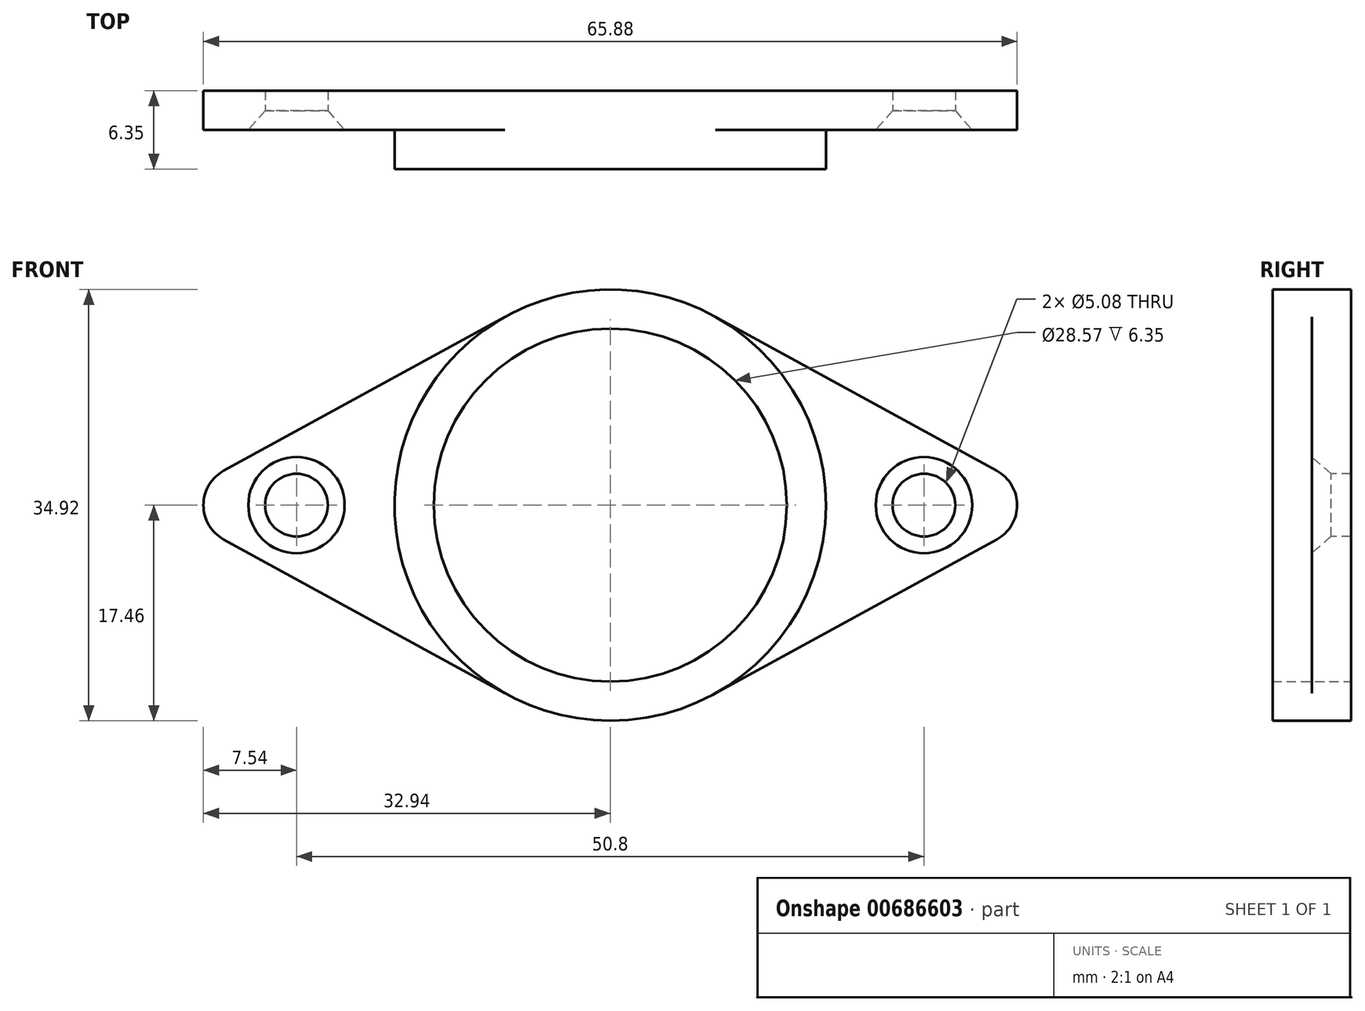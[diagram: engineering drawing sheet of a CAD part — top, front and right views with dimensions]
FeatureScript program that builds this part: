
annotation { "Feature Type Name" : "Feature", "Feature Type Description" : "" }
export const myFeature = defineFeature(function(context is Context, id is Id, definition is map)
    precondition{}
    {
        {
            var Q0;
            Q0=qCreatedBy(makeId("Front.planeOp"),FACE);
            var sketch = newSketch(context, id + "F0", { "sketchPlane" : qUnion([Q0])});
            skCircle(sketch, "E0", {"center": v(0, 0) * mm, "radius": 14.29 * mm});
            skCircle(sketch, "E1", {"center": v(0, 0) * mm, "radius": 17.46 * mm});
            skLineSegment(sketch, "E2", {"start": v(-8.53, 15.24) * mm, "end": v(-31.29, 2.79) * mm});
            skLineSegment(sketch, "E3", {"start": v(0, 8.62) * mm, "end": v(0, -7.37) * mm, "construction": true});
            skLineSegment(sketch, "E4", {"start": v(-7.8, 0) * mm, "end": v(5.65, 0) * mm, "construction": true});
            skLineSegment(sketch, "E5.MirrorCS", {"start": v(-8.53, -15.24) * mm, "end": v(-31.29, -2.79) * mm});
            skLineSegment(sketch, "E6.MirrorCS", {"start": v(8.53, -15.24) * mm, "end": v(31.29, -2.79) * mm});
            skLineSegment(sketch, "E7.MirrorCS", {"start": v(8.53, 15.24) * mm, "end": v(31.29, 2.79) * mm});
            skPoint(sketch, "E8.visualSharp", {"position": v(-36.38, 0) * mm});
            skArc(sketch, "E8.filletArc", {"start": v(-31.29, 2.79) * mm, "mid": v(-32.94, 0) * mm, "end": v(-31.29, -2.79) * mm});
            skPoint(sketch, "E9.visualSharp", {"position": v(36.38, 0) * mm});
            skArc(sketch, "E9.filletArc", {"start": v(31.29, -2.79) * mm, "mid": v(32.94, 0) * mm, "end": v(31.29, 2.79) * mm});
            skSolve(sketch);
        }
        {
            var Q0;
            Q0 = qSketchRegion(id + "F0", true);
            extrude(context, id + "F1", {"entities" : qUnion([Q0]), "depth" : 3.17 * mm, "offsetDistance" : 25.4 * mm});
        }
        {
            var Q0;
            Q0=makeQuery(id+"F0.imprint","IMPRINT",FACE,{"disambiguationData":[TD([[makeQuery(id+"F0.imprint","IMPRINT",EDGE,{"derivedFrom":sQuery(id+"F0.wireOp",EDGE,"E0")}),-1.0]])]});
            extrude(context, id + "F2", {"entities" : qUnion([Q0]), "operationType" : NewBodyOperationType.ADD, "depth" : 6.35 * mm, "offsetDistance" : 25.4 * mm});
        }
        {
            var Q0;
            {var subQ0=sQuery(id+"F0.wireOp",EDGE,"E5.MirrorCS");var subQ1=sQuery(id+"F0.wireOp",EDGE,"E2");var subQ2=sQuery(id+"F0.wireOp",EDGE,"E1");var subQ3=sQuery(id+"F0.wireOp",EDGE,"E6.MirrorCS");var subQ4=sQuery(id+"F0.wireOp",EDGE,"E7.MirrorCS");var subQ5=sQuery(id+"F0.wireOp",EDGE,"E8.filletArc");Q0=makeQuery(id+"F2.boolean.opBoolean","SPLIT",FACE,{"disambiguationData":[TD([makeQuery(id+"F1.opExtrude","SWEPT_FACE",FACE,{"disambiguationData":[OSD([subQ1])]})])],"derivedFrom":makeQuery(id+"F1.opExtrude","CAP_FACE",FACE,{"disambiguationData":[OSD([sQuery(id+"F0.wireOp",EDGE,"E0"),subQ2,subQ1,subQ0,subQ3,subQ4,subQ5,sQuery(id+"F0.wireOp",EDGE,"E9.filletArc")])],"isStart":false})});}
            var sketch = newSketch(context, id + "F3", { "sketchPlane" : qUnion([Q0])});
            skPoint(sketch, "E10", {"position": v(-25.4, 0) * mm});
            skPoint(sketch, "E11", {"position": v(25.4, 0) * mm});
            skSolve(sketch);
        }
        {
            var Q0;
            Q0=sQuery(id+"F3.wireOp",VERTEX,"E10");
            var Q1;
            Q1=sQuery(id+"F3.wireOp",VERTEX,"E11");
            var Q2;
            Q2=makeQuery(id+"F1.opExtrude","SWEPT_BODY",BODY,{"disambiguationData":[OSD([sQuery(id+"F0.wireOp",EDGE,"E0"),sQuery(id+"F0.wireOp",EDGE,"E1"),sQuery(id+"F0.wireOp",EDGE,"E2"),sQuery(id+"F0.wireOp",EDGE,"E5.MirrorCS"),sQuery(id+"F0.wireOp",EDGE,"E6.MirrorCS"),sQuery(id+"F0.wireOp",EDGE,"E7.MirrorCS"),sQuery(id+"F0.wireOp",EDGE,"E8.filletArc"),sQuery(id+"F0.wireOp",EDGE,"E9.filletArc")])]});
            hole(context, id + "F4", {"style" : HoleStyle.C_SINK, "endStyle" : HoleEndStyle.THROUGH, "holeDiameter" : 5.08 * mm, "cSinkDiameter" : 7.8 * mm, "cSinkAngle" : 82 * degree, "majorDiameter" : 6.35 * mm, "isTappedThrough" : true, "tappedDepth" : 12 * mm, "tapClearance" : 3, "locations" : qUnion([Q0, Q1]), "scope" : qUnion([Q2])});
        }
    });
